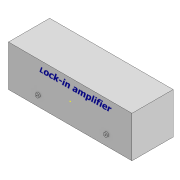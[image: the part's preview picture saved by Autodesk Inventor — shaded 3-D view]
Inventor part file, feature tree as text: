
AUTODESK INVENTOR PART (.ipt)
format: ipt  version: 2021 (Build 250183000, 183)  size: 97,792 bytes
history: native  units: mm
features: sketch x4, extrude x3, other x2
ambient origin geometry x8: Origin, YZ Plane, XZ Plane, XY Plane, X Axis, Y Axis, Z Axis, Center Point
bodies: Body1 (feature_tree)
feature tree (9):
  other  "Твердое тело1"
  extrude  "Выдавливание1"  Depth=30.0mm
  sketch  "Эскиз2"
  other  "РабПлоскость1"
  extrude  "Выдавливание2"  Depth=10.0mm
  extrude  "Выдавливание3"  Depth=10.0mm TaperAngle=0.0deg
  sketch  "Эскиз1"
  sketch  "Эскиз3"
  sketch  "Эскиз4"
